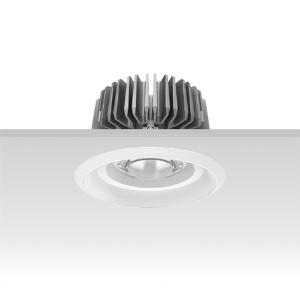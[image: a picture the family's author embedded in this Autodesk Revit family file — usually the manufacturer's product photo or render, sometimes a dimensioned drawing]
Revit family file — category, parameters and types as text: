
# Revit family: 3f_filippi_-_3f_reno_bianco_ellittico_3f_filippi_-_30495_-_3f_reno_150_wh_3000-840_dali_ell
name_source: partatom
category: Lighting Fixtures
units: mm (PartAtom-declared; Revit-internal decimal feet)

## family parameters
Cut with Voids When Loaded = No
Host = Face
Light Source = No
Part Type = Normal
Room Calculation Point = No
Round Connector Dimension = Use Diameter
Shared = No

## types (1)
- 3F Filippi - 3F Reno Bianco Ellittico (1 x LED, 2871 lm, 28 W, 4000 K)
    Apparent Load = 28 VA
    Approval mark = CE
    CIE Flux Codes = 74 98 100 100 100
    Color Rendering = 80
    Color Temperature = 4000 K
    Control Gear = Electronic transformer
    Default Elevation = 1800 mm
    Description = ILLUMINOTECHNICAL
Luminous efficiency 100% (DLOR 100%, ULOR 0%).
Initial luminous flux of the luminaire 2871 lm.
Direct symmetric elliptical distribution.
Installation Interdistance Transv.D = 0.77 x hu - Long.D = 1.47 x hu.
Tabular UGR (CIE 117 - 4H-8H; S=0.25H; 70/50/20): RUG 21 - 25.4.
Beam angle: 63° - 92°.
Luminous efficacy 103 lm/W.
Lifetime (L90/B10): 30000 h. (tq+25°C)
Lifetime (L85/B10): 50000 h. (tq+25°C)
Lifetime (L70/B10): 80000 h. (tq+25°C)
Sudden decreased luminous flux after 50000 hours: 0% (C0).
Photobiological safety in compliance with IEC/TR 62778: RG1 low risk, (IEC 62471).
In compliance with IEC/EN 62722-2-1 - IEC/EN 62717 standards.

SOURCE
Compact LED module 3000/840.
Energy efficiency class (UE 2019/2020 - UE 2019/2015): D.
CIE 13.3 Colour rendering index: CRI >80 (R9 <50%).
IES TM-30 Fidelity Index: Rf = 84 Rg = 95.
CCT nominal colour temperature 4000 K.
Colour initial tolerance (MacAdam): SDCM 3.
Zhaga Book 3 compliant.

MECHANICAL
Passive heat dissipator in die-casting aluminium, oversized, for optimum thermal management of the LED module.
Parabolic element with graduated/concentric rings in white polycarbonate.
Internal specular metallic louvre to optimise control of the luminous flux in polycarbonate.
Transparent external lens with glossy and satin differentiated surfaces, with a cooling and anti-insect system in methacrylate (PMMA).
Fastening spring clips in stainless steel.
Dimensions: diameter 166 mm, height 107 mm. Weight 1.3 kg.
IP44 protection degree for exposed part, IP20 for recessed part.
Mechanical strength to impacts IK04 (0.5 joule).
Glow-wire test resistance 650°C.

ELECTRICAL
Wiring on a separate unit.
Halogen Free DALI-2 DATI (Parts 251, 252, 253), PUSH-DIM, electronic wiring 230V-50/60Hz, power factor 0.97 at full load, THD <25%, constant output current, SELV, class II, 1 driver, 1 DALI addresse.
Power of the luminaire 28 W.
ENEC - CE.
SAFE FLICKER: PstLM=<1 and SVM=<0.4 (IEC TR 61547-1 and IEC TR 63158), to ensure a more comfortable and safe light.
Luminaire compliant with EN 60598-2-22 for power supply from a centralised emergency system CPSS (Central Power Supply System), not incorporated in the luminaire - high risk areas excluded. The default power and flux are 100% in AC and 100% in DC.
Ambient temperature from 0°C to +25°C.
Temperature class T6 max 85°C.
Relative humidity UR: <85%.

INSTALLATION
Pull-up recessed fitting.
False ceiling carving: 150 mm.
All accessories dedicated to this product are available on the Catalog and on our website www.3F-Filippi.com.

APPLICATIONS
Environments: architectural, commercial, exhibition areas, transit areas, corridors, shops, display windows, service areas.
In false ceilings with narrow voids.

LIGHT MANAGEMENT
Recommended minimum setting: 10%.
The luminaire, equipped with (DALI-2 DATI) driver, can be controlled manually with 3F Easy Dim technology or automatically/manually with wired or wireless DALI/D2D control systems.
The D2D driver guarantees interoperability with other devices with the same certification by making the following information available:
Device Data (Part 251), Energy Report (Part 252), Diagnosis & Maintenance (Part 253).
In electrical systems without a regulation system (manual or automatic) and DALI bus, a suitable jumper must be made on the DA-DA terminals of the appliance.

WARNING
Luminaire designed for disposal/recycling at end-of-life.
Replaceable (LED only) light source by a professional. Replaceable control gear by a professional.
    Height = 0 mm  [stored 0 ft]
    Lamp = 1 x LED
    Lamp Light Flux = 2871 lm
    Lamp Power = 28 W
    Lamp count = 1
    Length = 166 mm
    Lifetime = 50000 h
    Luminous efficacy = 103 lm/W
    Manufacturer = 3F Filippi
    ModVariant = No
    Model = 3F Filippi - 30495 - 3F Reno 150 WH 3000-840 DALI ELL
    Mounting Place = Ceiling
    Mounting Type = Recessed
    Number of Poles = 1
    OnlyDefault = Yes
    Power Factor = 1
    Product Name = 3F Filippi - 3F Reno Bianco Ellittico
    Product group = recessed luminaire
    ProductGroupID = 4
    Protection Class = Protection class II
    Protection Degree = IP 20
    RLX_Detail_Level = 1
    RLX_Emergency_Light_Flux = 0 lm
    RLX_Emergency_Type = 0
    RLX_Emergency_Type_DB = No
    RlxData = <blob elided: 86381 chars, md5=b1fc8e9a>
    Socket = socket
    Standby Power = 0 W
    System Light Flux = 2871 lm
    System Power = 28 W
    Type Comments = Product without accessories
    Type Image = 3ffilippi_3f_reno_150_wh_3000_4000.jpg
    URL = http://relux.com
    VarID = ---
    Voltage = 0 V
    Weight = 0.00 kg
    Width = 0 mm  [stored 0 ft]

note: [stored X ft] marks values corroborated as IEEE doubles in the binary element streams (Revit-internal decimal feet)

## geometry (parser evidence)
native form markers: Blend x4, Sweep x11
no freeform markers — native parametric forms only
